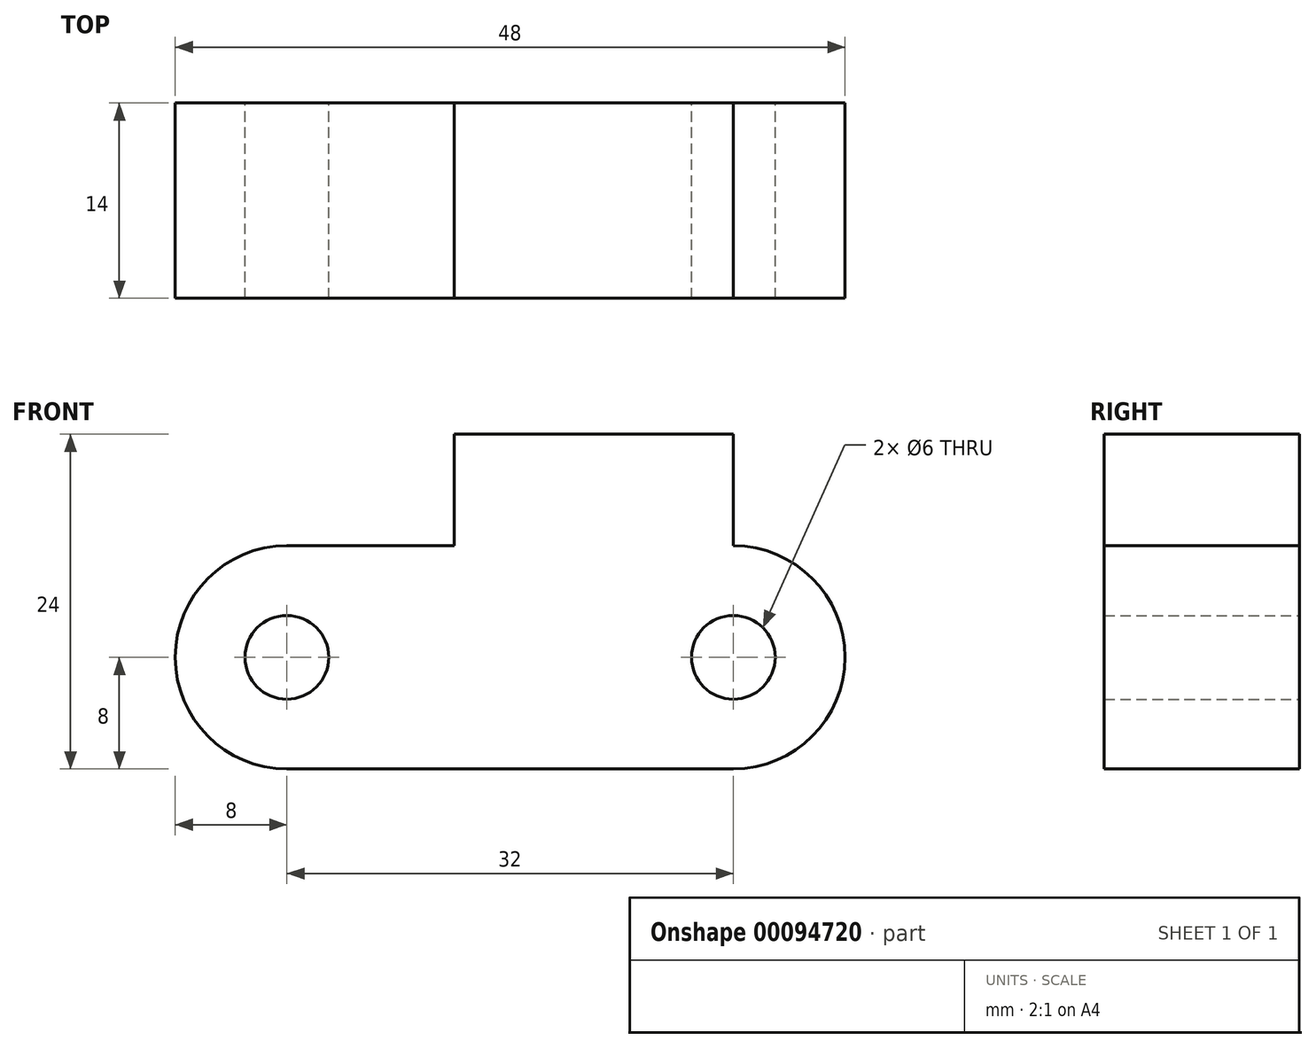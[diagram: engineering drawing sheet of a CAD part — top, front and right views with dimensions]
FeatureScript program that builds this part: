
annotation { "Feature Type Name" : "Feature", "Feature Type Description" : "" }
export const myFeature = defineFeature(function(context is Context, id is Id, definition is map)
    precondition{}
    {
        {
            var Q0;
            Q0=qCreatedBy(makeId("Front.planeOp"),FACE);
            var sketch = newSketch(context, id + "F0", { "sketchPlane" : qUnion([Q0])});
            skCircle(sketch, "E0", {"center": v(-16, 0) * mm, "radius": 3 * mm});
            skCircle(sketch, "E1", {"center": v(16, 0) * mm, "radius": 3 * mm});
            skLineSegment(sketch, "E2", {"start": v(-16, 0) * mm, "end": v(16, 0) * mm});
            skArc(sketch, "E3.0.startCap", {"start": v(-16, -8) * mm, "mid": v(-24, 0) * mm, "end": v(-16, 8) * mm});
            skArc(sketch, "E3.0.endCap", {"start": v(16, 8) * mm, "mid": v(24, 0) * mm, "end": v(16, -8) * mm});
            skLineSegment(sketch, "E3.0.left", {"start": v(-16, 8) * mm, "end": v(-4, 8) * mm});
            skLineSegment(sketch, "E3.0.right", {"start": v(-16, -8) * mm, "end": v(16, -8) * mm});
            skLineSegment(sketch, "E4", {"start": v(-4, 16) * mm, "end": v(16, 16) * mm});
            skLineSegment(sketch, "E5", {"start": v(16, 16) * mm, "end": v(16, 8) * mm});
            skLineSegment(sketch, "E6", {"start": v(-4, 16) * mm, "end": v(-4, 8) * mm});
            skSolve(sketch);
        }
        {
            var Q0;
            Q0 = qSketchRegion(id + "F0", true);
            extrude(context, id + "F1", {"entities" : qUnion([Q0]), "depth" : 14 * mm});
        }
    });
